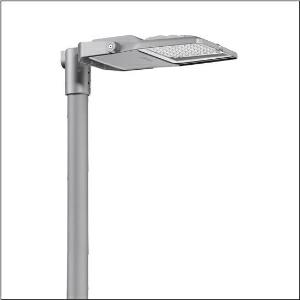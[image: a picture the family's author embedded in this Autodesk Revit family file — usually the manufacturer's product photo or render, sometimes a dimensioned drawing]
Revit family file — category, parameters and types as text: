
# Revit family: floodlight_fl_21_iq_mini___pl64_5xa7771c4e3a_84b6
name_source: partatom
category: Lighting Fixtures
units: mm (PartAtom-declared; Revit-internal decimal feet)

## family parameters
Cut with Voids When Loaded = No
Host = Face
Light Source = No
Part Type = Normal
Room Calculation Point = No
Round Connector Dimension = Use Diameter
Shared = No

## types (1)
- --- (1 x LED, 12280 lm, 87.2 W, 4000K)
    Apparent Load = 87 VA
    CIE Flux Codes = 28 80 98 100 100
    Color Rendering = 70
    Color Temperature = 4000K
    Default Elevation = 1800 mm
    Description = Floodlight FL 21 iQ mini, floodlight, primary light control with lens, of PMMA, primary optical cover: protective disc, of toughened safety glass, transparent, light distribution: PL64, light emission: direct distribution, installation type: surface-mounted, LED, High Power LED, rated luminous flux: 12.280lm, luminous efficacy: 141lm/W, light colour: 740, colour temperature: 4000K, control: Auto-Match, Temp-Guard, Lumen-Switch, Night-Set, Smart-Wire, Light-Fading, Desk-Remote (wireless, voltage-free reading and setting of iQ features in the workshop via application-optimized NFC function/RFID function), optimised constant luminous flux control (CLO 2.0), with terminal, 6-pole, mains connection: 220..240V, AC, 50/60Hz, start of lifetime: 87W, end of service life: 92W, reduction: 40W, luminaire housing, of diecast aluminium, powder-coated, Siteco® metallic grey (DB 702S), corrosivity category C5 mid according to DIN EN ISO 12944, sealing non-destructively replaceable, please order mast flange separately, mast bracket, of steel, galvanised, powder-coated, Siteco® metallic grey (DB 702S), protection rating (complete): IP66, insulation class (complete): insulation class II (safety insulation), certification: CE, ENEC, VDE, protection symbol: D, impact resistance: IK08, permissible operating ambient temperature: -40..+40°C, permissible operating ambient temperature for outdoor applications: -40..+50°C, standard: DIN EN 12944, LABS conformity tested according to VDMA 24364:2018-05, packaging unit: 1 piece

Light Distribution: PL64
    Height = 70 mm
    Lamp = 1 x LED
    Lamp Light Flux = 12280 lm
    Lamp Power = 87.2 W
    Lamp count = 1
    Length = 485 mm
    Luminous efficacy = 141 lm/W
    Manufacturer = Siteco
    ModVariant = No
    Model = 5XA7771C4E3A
    Number of Poles = 1
    OnlyDefault = Yes
    Power Factor = 1
    Product Name = Floodlight FL 21 iQ mini | PL64
    Product group = floodlight | pylon annexe
    ProductGroupID = 6200
    Protection Class = Protection class II
    Protection Degree = IP 66
    RLX_Detail_Level = 1
    RLX_Emergency_Light_Flux = 0 lm
    RLX_Emergency_Type = 0
    RLX_Emergency_Type_DB = No
    RlxData = <blob elided: 101329 chars, md5=e04a3476>
    Socket = socket
    Standby Power = 0 W
    System Light Flux = 12280 lm
    System Power = 87 W
    Type Comments = factory setting: luminous flux: 100 % | dim-lin: 254 | 456 mA
    Type Image = l_1007125.jpg
    URL = http://relux.com
    VarID = @adj_136839
    Voltage = 0 V
    Weight = 0.00 kg
    Width = 337 mm

## geometry (parser evidence)
native form markers: Blend x4, Sweep x11
no freeform markers — native parametric forms only
